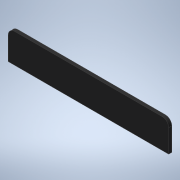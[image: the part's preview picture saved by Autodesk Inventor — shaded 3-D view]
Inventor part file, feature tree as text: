
AUTODESK INVENTOR PART (.ipt)
format: ipt  version: 2020 (Build 240168000, 168)  size: 102,912 bytes
history: native  units: mm
features: other x1, extrude x1, fillet x1
ambient origin geometry x8: Origin, YZ Plane, XZ Plane, XY Plane, X Axis, Y Axis, Z Axis, Center Point
bodies: Body1 (feature_tree)
feature tree (3):
  other  "實體1"
  extrude  "擠出1"  Depth=23.0mm
  fillet  "圓角1"  Radius=126.0mm
